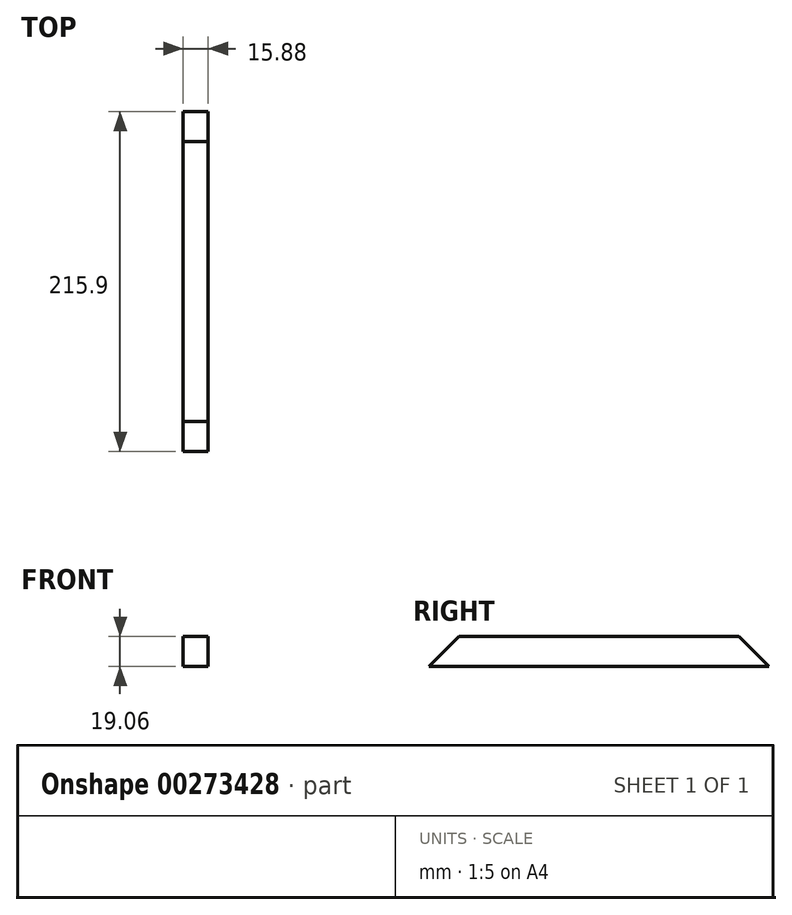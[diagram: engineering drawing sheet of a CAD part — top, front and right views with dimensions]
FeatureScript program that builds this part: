
annotation { "Feature Type Name" : "Feature", "Feature Type Description" : "" }
export const myFeature = defineFeature(function(context is Context, id is Id, definition is map)
    precondition{}
    {
        {
            var Q0;
            Q0=qCreatedBy(makeId("Right.planeOp"),FACE);
            var sketch = newSketch(context, id + "F0", { "sketchPlane" : qUnion([Q0])});
            skLineSegment(sketch, "E0.bottom", {"start": v(-107.95, 9.52) * mm, "end": v(107.95, 9.52) * mm});
            skLineSegment(sketch, "E0.top", {"start": v(-107.95, -9.53) * mm, "end": v(107.95, -9.52) * mm});
            skLineSegment(sketch, "E0.left", {"start": v(-107.95, 9.53) * mm, "end": v(-107.95, -9.53) * mm});
            skLineSegment(sketch, "E0.right", {"start": v(107.95, 9.53) * mm, "end": v(107.95, -9.53) * mm});
            skSolve(sketch);
        }
        {
            var Q0;
            Q0=makeQuery(id+"F0.imprint","IMPRINT",FACE,{"disambiguationData":[TD([[makeQuery(id+"F0.imprint","IMPRINT",EDGE,{"derivedFrom":sQuery(id+"F0.wireOp",EDGE,"E0.bottom")}),-1.0]])]});
            extrude(context, id + "F1", {"entities" : qUnion([Q0]), "endBound" : BoundingType.SYMMETRIC, "depth" : 15.88 * mm});
        }
        {
            var Q0;
            Q0=makeQuery(id+"F1.opExtrude","SWEPT_EDGE",EDGE,{"disambiguationData":[OSD([sQuery(id+"F0.wireOp",EDGE,"E0.bottom"),sQuery(id+"F0.wireOp",EDGE,"E0.left")])]});
            chamfer(context, id + "F2", {"entities" : qUnion([Q0]), "chamferType" : ChamferType.OFFSET_ANGLE, "width" : 19.05 * mm, "oppositeDirection" : false, "angle" : 45 * degree, "tangentPropagation" : true});
        }
        {
            var Q0;
            Q0=makeQuery(id+"F1.opExtrude","SWEPT_EDGE",EDGE,{"disambiguationData":[OSD([sQuery(id+"F0.wireOp",EDGE,"E0.bottom"),sQuery(id+"F0.wireOp",EDGE,"E0.right")])]});
            chamfer(context, id + "F3", {"entities" : qUnion([Q0]), "chamferType" : ChamferType.OFFSET_ANGLE, "width" : 19.05 * mm, "oppositeDirection" : false, "angle" : 45 * degree, "tangentPropagation" : true});
        }
    });
